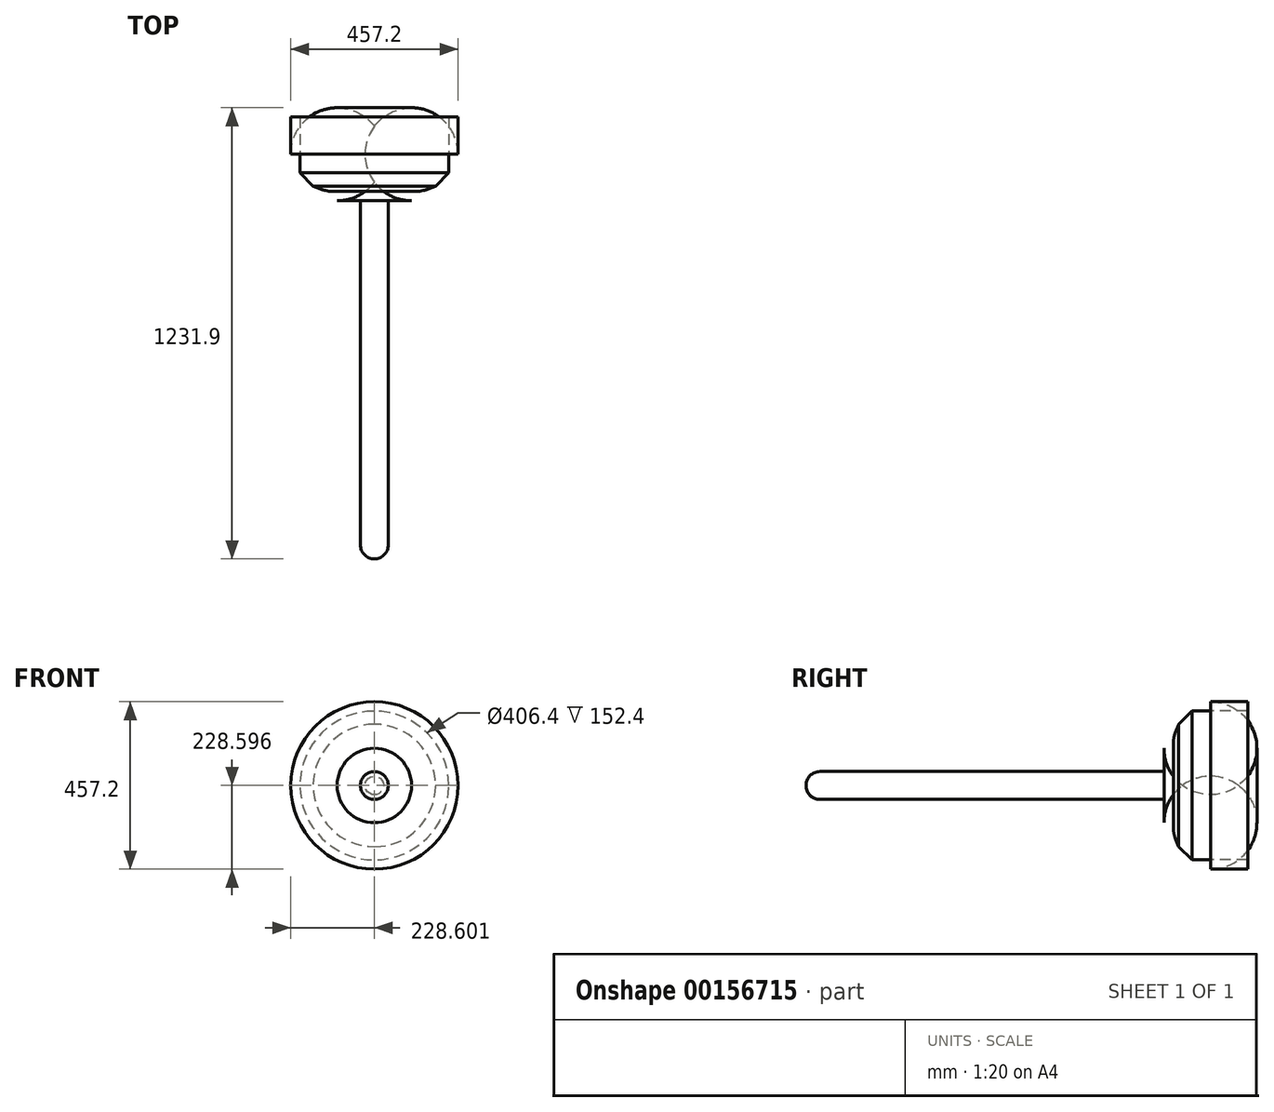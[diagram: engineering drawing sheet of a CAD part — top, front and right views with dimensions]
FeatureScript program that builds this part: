
annotation { "Feature Type Name" : "Feature", "Feature Type Description" : "" }
export const myFeature = defineFeature(function(context is Context, id is Id, definition is map)
    precondition{}
    {
        {
            var Q0;
            Q0=qCreatedBy(makeId("Front.planeOp"),FACE);
            var sketch = newSketch(context, id + "F0", { "sketchPlane" : qUnion([Q0])});
            skCircle(sketch, "E0", {"center": v(-33.57, 28.18) * mm, "radius": 38.1 * mm});
            skSolve(sketch);
        }
        {
            var Q0;
            Q0 = qSketchRegion(id + "F0", true);
            extrude(context, id + "F1", {"entities" : qUnion([Q0]), "depth" : 977.9 * mm});
        }
        {
            var Q0;
            Q0=makeQuery(id+"F1.opExtrude","CAP_EDGE",EDGE,{"disambiguationData":[OSD([sQuery(id+"F0.wireOp",EDGE,"E0")])],"isStart":false});
            fillet(context, id + "F2", {"entities" : qUnion([Q0]), "radius" : 38.1 * mm, "tangentPropagation" : true, "allowEdgeOverflow" : false});
        }
        {
            var Q0;
            Q0=makeQuery(id+"F1.opExtrude","CAP_FACE",FACE,{"disambiguationData":[OSD([sQuery(id+"F0.wireOp",EDGE,"E0")])],"isStart":true});
            var sketch = newSketch(context, id + "F3", { "sketchPlane" : qUnion([Q0])});
            skCircle(sketch, "E1", {"center": v(33.57, 28.18) * mm, "radius": 228.6 * mm});
            skSolve(sketch);
        }
        {
            var Q0;
            Q0 = qSketchRegion(id + "F3", true);
            extrude(context, id + "F4", {"entities" : qUnion([Q0]), "depth" : 228.6 * mm});
        }
        {
            var Q0;
            Q0=makeQuery(id+"F4.opExtrude","CAP_FACE",FACE,{"disambiguationData":[OSD([sQuery(id+"F3.wireOp",EDGE,"E1")])],"isStart":false});
            shell(context, id + "F5", {"entities" : qUnion([Q0]), "thickness" : 25.4 * mm});
        }
        {
            var Q0;
            {var subQ0=sQuery(id+"F3.wireOp",EDGE,"E1");Q0=makeQuery(id+"F5.opShell","OFFSET_EDGE",EDGE,{"disambiguationData":[OSD([subQ0]),TDD([makeQuery(id+"F4.opExtrude","CAP_EDGE",EDGE,{"disambiguationData":[OSD([subQ0])],"isStart":true})])]});}
            chamfer(context, id + "F6", {"entities" : qUnion([Q0]), "width" : 50.8 * mm, "tangentPropagation" : true});
        }
        {
            var Q0;
            {var subQ0=sQuery(id+"F3.wireOp",EDGE,"E1");Q0=makeQuery(id+"F5.opShell","OFFSET_FACE",FACE,{"disambiguationData":[OSD([subQ0]),TDD([makeQuery(id+"F4.opExtrude","CAP_FACE",FACE,{"disambiguationData":[OSD([subQ0])],"isStart":true})])]});}
            chamfer(context, id + "F7", {"entities" : qUnion([Q0]), "width" : 50.8 * mm, "tangentPropagation" : true});
        }
        {
            var Q0;
            Q0=makeQuery(id+"F4.opExtrude","CAP_EDGE",EDGE,{"disambiguationData":[OSD([sQuery(id+"F3.wireOp",EDGE,"E1")])],"isStart":true});
            fillet(context, id + "F8", {"entities" : qUnion([Q0]), "radius" : 127 * mm, "tangentPropagation" : true, "allowEdgeOverflow" : false});
        }
        {
            var Q0;
            {var subQ0=sQuery(id+"F3.wireOp",EDGE,"E1");var subQ1=makeQuery(id+"F5.opShell","OFFSET_FACE",FACE,{"disambiguationData":[OSD([subQ0]),TDD([makeQuery(id+"F4.opExtrude","CAP_FACE",FACE,{"disambiguationData":[OSD([subQ0])],"isStart":true})])]});Q0=makeQuery(id+"F7.opChamfer","BLEND_EDGE",EDGE,{"blendedFrom":[makeQuery(id+"F6.opChamfer","BLEND_EDGE",EDGE,{"blendedFrom":[makeQuery(id+"F5.opShell","OFFSET_EDGE",EDGE,{"disambiguationData":[OSD([subQ0]),TDD([makeQuery(id+"F4.opExtrude","CAP_EDGE",EDGE,{"disambiguationData":[OSD([subQ0])],"isStart":true})])]}),subQ1],"blendedInto":[subQ1]}),subQ1],"blendedInto":[subQ1]});}
            chamfer(context, id + "F9", {"entities" : qUnion([Q0]), "width" : 50.8 * mm, "tangentPropagation" : true});
        }
        {
            var Q0;
            Q0=makeQuery(id+"F9.opChamfer","BLEND_FACE",FACE,{"disambiguationData":[OSD([sQuery(id+"F3.wireOp",EDGE,"E1")])]});
            fillet(context, id + "F10", {"entities" : qUnion([Q0]), "radius" : 76.2 * mm, "tangentPropagation" : true, "allowEdgeOverflow" : false});
        }
    });
